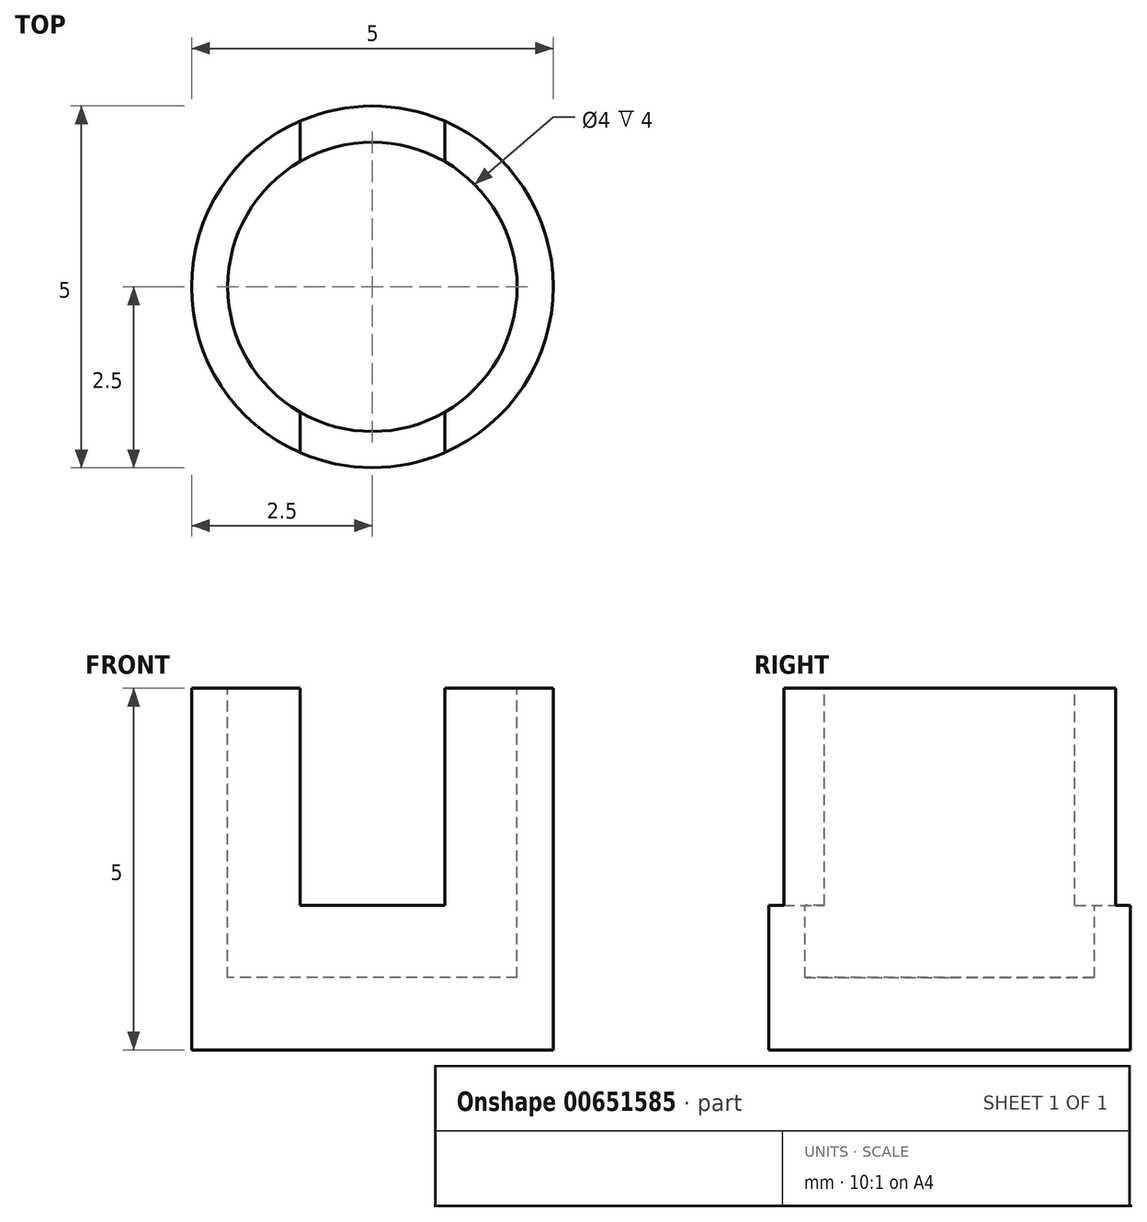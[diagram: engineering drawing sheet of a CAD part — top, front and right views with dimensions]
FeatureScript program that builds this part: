
annotation { "Feature Type Name" : "Feature", "Feature Type Description" : "" }
export const myFeature = defineFeature(function(context is Context, id is Id, definition is map)
    precondition{}
    {
        {
            var Q0;
            Q0=qCreatedBy(makeId("Top.planeOp"),FACE);
            var sketch = newSketch(context, id + "F0", { "sketchPlane" : qUnion([Q0])});
            skCircle(sketch, "E0", {"center": v(0, 0) * mm, "radius": 2.5 * mm});
            skSolve(sketch);
        }
        {
            var Q0;
            Q0=makeQuery(id+"F0.imprint","IMPRINT",FACE,{"disambiguationData":[TD([[makeQuery(id+"F0.imprint","IMPRINT",EDGE,{"derivedFrom":sQuery(id+"F0.wireOp",EDGE,"E0")}),1.0]])]});
            extrude(context, id + "F1", {"entities" : qUnion([Q0]), "depth" : 5 * mm});
        }
        {
            var Q0;
            Q0=makeQuery(id+"F1.opExtrude","CAP_FACE",FACE,{"disambiguationData":[OSD([sQuery(id+"F0.wireOp",EDGE,"E0")])],"isStart":false});
            var sketch = newSketch(context, id + "F2", { "sketchPlane" : qUnion([Q0])});
            skCircle(sketch, "E1", {"center": v(0, 0) * mm, "radius": 2 * mm});
            skSolve(sketch);
        }
        {
            var Q0;
            Q0=qSketchRegion(id+"F2",true);
            extrude(context, id + "F3", {"entities" : qUnion([Q0]), "operationType" : NewBodyOperationType.REMOVE, "oppositeDirection" : true, "depth" : 4 * mm});
        }
        {
            var Q0;
            Q0=makeQuery(id+"F1.opExtrude","CAP_FACE",FACE,{"disambiguationData":[OSD([sQuery(id+"F0.wireOp",EDGE,"E0")])],"isStart":false});
            var sketch = newSketch(context, id + "F4", { "sketchPlane" : qUnion([Q0])});
            skLineSegment(sketch, "E2.bottom", {"start": v(1, -3.33) * mm, "end": v(-1, -3.33) * mm});
            skLineSegment(sketch, "E2.top", {"start": v(1, -0.67) * mm, "end": v(-1, -0.67) * mm});
            skLineSegment(sketch, "E2.left", {"start": v(1, -3.33) * mm, "end": v(1, -0.67) * mm});
            skLineSegment(sketch, "E2.right", {"start": v(-1, -3.33) * mm, "end": v(-1, -0.67) * mm});
            skPoint(sketch, "E2.middle", {"position": v(0, -2) * mm});
            skSolve(sketch);
        }
        {
            var Q0;
            {var subQ0=sQuery(id+"F4.wireOp",EDGE,"E2.left");var subQ1=makeQuery(id+"F1.opExtrude","CAP_EDGE",EDGE,{"disambiguationData":[OSD([sQuery(id+"F0.wireOp",EDGE,"E0")])],"isStart":false});var subQ2=makeQuery(id+"F4.imprint","INTERSECT",VERTEX,{"derivedFrom":[subQ1,subQ0]});Q0=makeQuery(id+"F4.imprint","IMPRINT",FACE,{"disambiguationData":[TD([[makeQuery(id+"F4.imprint","IMPRINT",EDGE,{"disambiguationData":[TD([[subQ2,-1.0]])],"derivedFrom":subQ0}),1.0]])]});}
            extrude(context, id + "F5", {"entities" : qUnion([Q0]), "operationType" : NewBodyOperationType.REMOVE, "oppositeDirection" : true, "depth" : 3 * mm});
        }
        {
            var Q0;
            Q0=makeQuery(id+"F1.opExtrude","CAP_FACE",FACE,{"disambiguationData":[OSD([sQuery(id+"F0.wireOp",EDGE,"E0")])],"isStart":false});
            var sketch = newSketch(context, id + "F6", { "sketchPlane" : qUnion([Q0])});
            skLineSegment(sketch, "E3.bottom", {"start": v(1, 1.09) * mm, "end": v(-1, 1.08) * mm});
            skLineSegment(sketch, "E3.top", {"start": v(1, 2.92) * mm, "end": v(-1, 2.92) * mm});
            skLineSegment(sketch, "E3.left", {"start": v(1, 1.08) * mm, "end": v(1, 2.92) * mm});
            skLineSegment(sketch, "E3.right", {"start": v(-1, 1.08) * mm, "end": v(-1, 2.92) * mm});
            skPoint(sketch, "E3.middle", {"position": v(0, 2) * mm});
            skSolve(sketch);
        }
        {
            var Q0;
            Q0=qSketchRegion(id+"F6",true);
            extrude(context, id + "F7", {"entities" : qUnion([Q0]), "operationType" : NewBodyOperationType.REMOVE, "oppositeDirection" : true, "depth" : 3 * mm});
        }
    });
